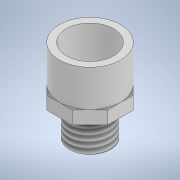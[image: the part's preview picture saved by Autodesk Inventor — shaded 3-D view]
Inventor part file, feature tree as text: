
AUTODESK INVENTOR PART (.ipt)
format: ipt  version: 2022 (Build 260153000, 153)  size: 161,280 bytes
history: native  units: mm
features: extrude x6, sketch x6, other x1, plane x1, thread x1
ambient origin geometry x8: Origin, YZ Plane, XZ Plane, XY Plane, X Axis, Y Axis, Z Axis, Center Point
bodies: Body1 (feature_tree)
feature tree (15):
  other  "Sólido1"
  extrude  "Extrusión1"  Depth=27.76mm
  extrude  "Extrusión2"  Depth=22.6mm
  plane  "Plano de trabajo2"
  extrude  "Extrusión4"  Depth=5.75mm
  extrude  "Extrusión5"  Depth=5.75mm
  extrude  "Extrusión6"  Depth=5.75mm
  extrude  "Extrusión7"  Depth=5.97mm TaperAngle=0.0deg
  thread  "Rosca2"  [1 undecoded]
  sketch  "Boceto1"  dims[d0=21.4mm d1=27.76mm]
  sketch  "Boceto2"  dims[d2=22.6mm d3=0.0mm d5=5.75mm]
  sketch  "Boceto4"  dims[d6=5.75mm d7=5.75mm]
  sketch  "Boceto5"  dims[d8=5.75mm d9=5.75mm]
  sketch  "Boceto6"  dims[d10=5.75mm d11=5.75mm]
  sketch  "Boceto7"  dims[d12=5.75mm d13=5.97mm d14=0.0mm d17=-18.5mm d18=13.6mm d19=18.97mm d20=0.0mm d21=18.97mm d22=0.0mm d25=13.4mm d26=18.6mm d27=18.97mm d28=0.0mm d29=13.6mm d30=18.97mm d31=0.0mm d32=14.87mm d33=0.0mm]
note: 1 required parameter value undecoded (feature->parameter linkage not recoverable at this tier; creation-order binding heuristic only, values carry confidence <= 0.55)
